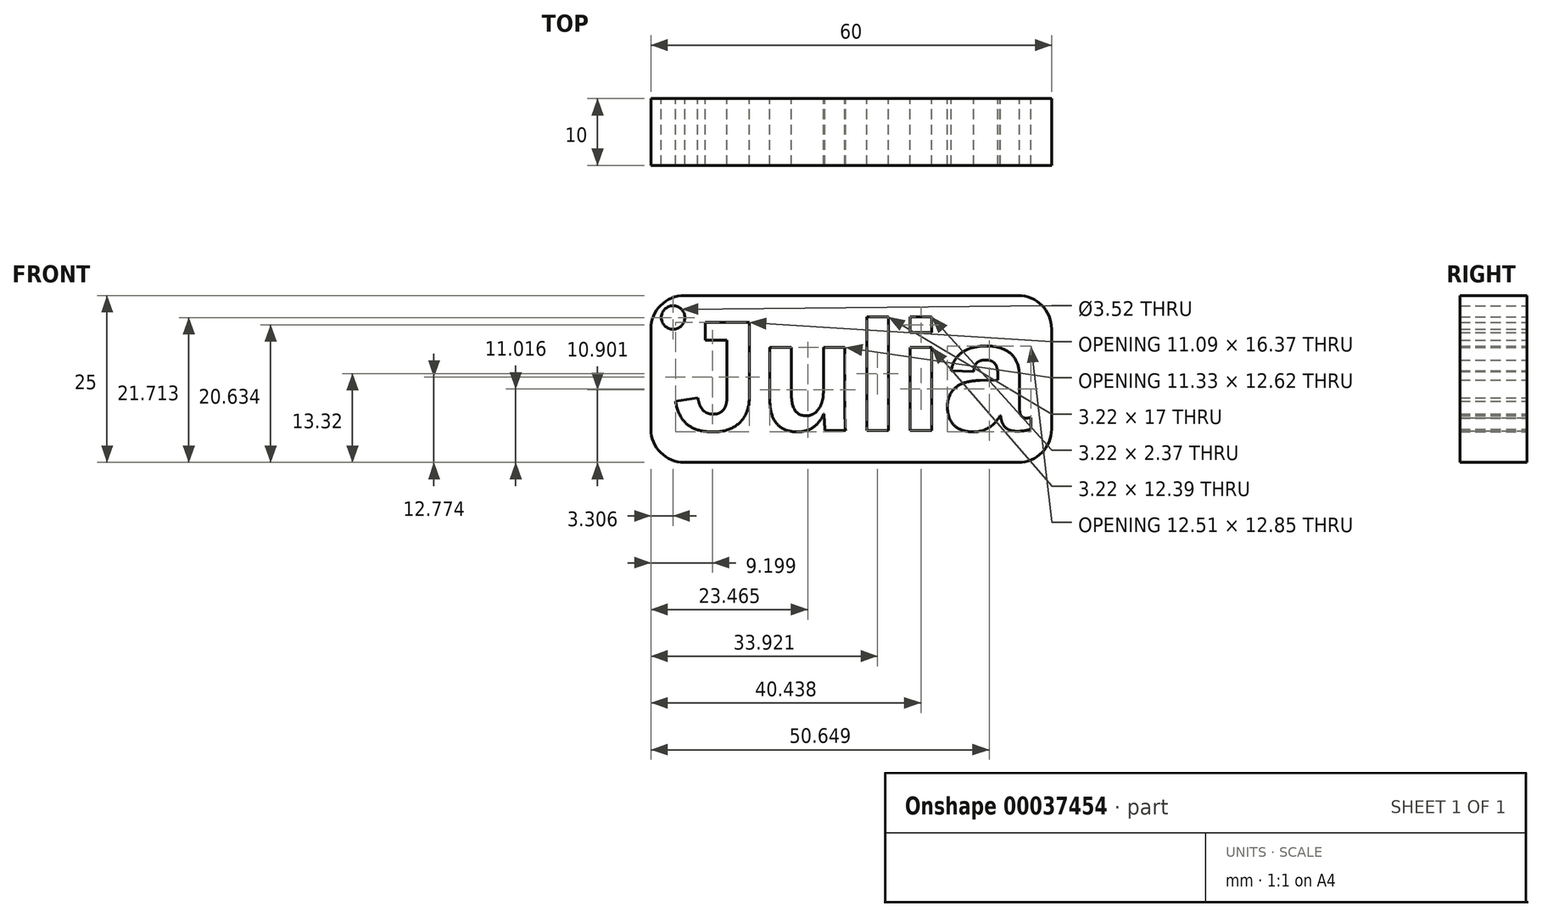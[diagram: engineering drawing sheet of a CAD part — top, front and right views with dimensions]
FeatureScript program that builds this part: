
annotation { "Feature Type Name" : "Feature", "Feature Type Description" : "" }
export const myFeature = defineFeature(function(context is Context, id is Id, definition is map)
    precondition{}
    {
        {
            var Q0;
            Q0=qCreatedBy(makeId("Front.planeOp"),FACE);
            var sketch = newSketch(context, id + "F0", { "sketchPlane" : qUnion([Q0])});
            skLineSegment(sketch, "E0.bottom", {"start": v(-32.1, 9.56) * mm, "end": v(27.9, 9.56) * mm});
            skLineSegment(sketch, "E0.top", {"start": v(-32.1, -15.44) * mm, "end": v(27.9, -15.44) * mm});
            skLineSegment(sketch, "E0.left", {"start": v(-32.1, 9.56) * mm, "end": v(-32.1, -15.44) * mm});
            skLineSegment(sketch, "E0.right", {"start": v(27.9, 9.56) * mm, "end": v(27.9, -15.44) * mm});
            skText(sketch, "E1", { "text": "Julia", "fontName": "Arimo-Bold.ttf"});
            skCircle(sketch, "E2", {"center": v(-28.8, 6.27) * mm, "radius": 1.76 * mm});
            const initialGuessF0  = {"E1": [-0.0288, -0.01062, 1, 0, 0.01689]};
            skSetInitialGuess(sketch, initialGuessF0);
            skSolve(sketch);
        }
        {
            var Q0;
            Q0 = qSketchRegion(id + "F0", true);
            extrude(context, id + "F1", {"entities" : qUnion([Q0]), "depth" : 10 * mm});
        }
        {
            var Q0;
            Q0=makeQuery(id+"F1.opExtrude","SWEPT_EDGE",EDGE,{"disambiguationData":[OSD([sQuery(id+"F0.wireOp",EDGE,"E0.bottom"),sQuery(id+"F0.wireOp",EDGE,"E0.left")])]});
            var Q1;
            Q1=makeQuery(id+"F1.opExtrude","SWEPT_EDGE",EDGE,{"disambiguationData":[OSD([sQuery(id+"F0.wireOp",EDGE,"E0.top"),sQuery(id+"F0.wireOp",EDGE,"E0.right")])]});
            var Q2;
            Q2=makeQuery(id+"F1.opExtrude","SWEPT_EDGE",EDGE,{"disambiguationData":[OSD([sQuery(id+"F0.wireOp",EDGE,"E0.bottom"),sQuery(id+"F0.wireOp",EDGE,"E0.right")])]});
            var Q3;
            Q3=makeQuery(id+"F1.opExtrude","SWEPT_EDGE",EDGE,{"disambiguationData":[OSD([sQuery(id+"F0.wireOp",EDGE,"E0.top"),sQuery(id+"F0.wireOp",EDGE,"E0.left")])]});
            fillet(context, id + "F2", {"entities" : qUnion([Q0, Q1, Q2, Q3]), "radius" : 5 * mm, "tangentPropagation" : true, "allowEdgeOverflow" : false});
        }
    });
